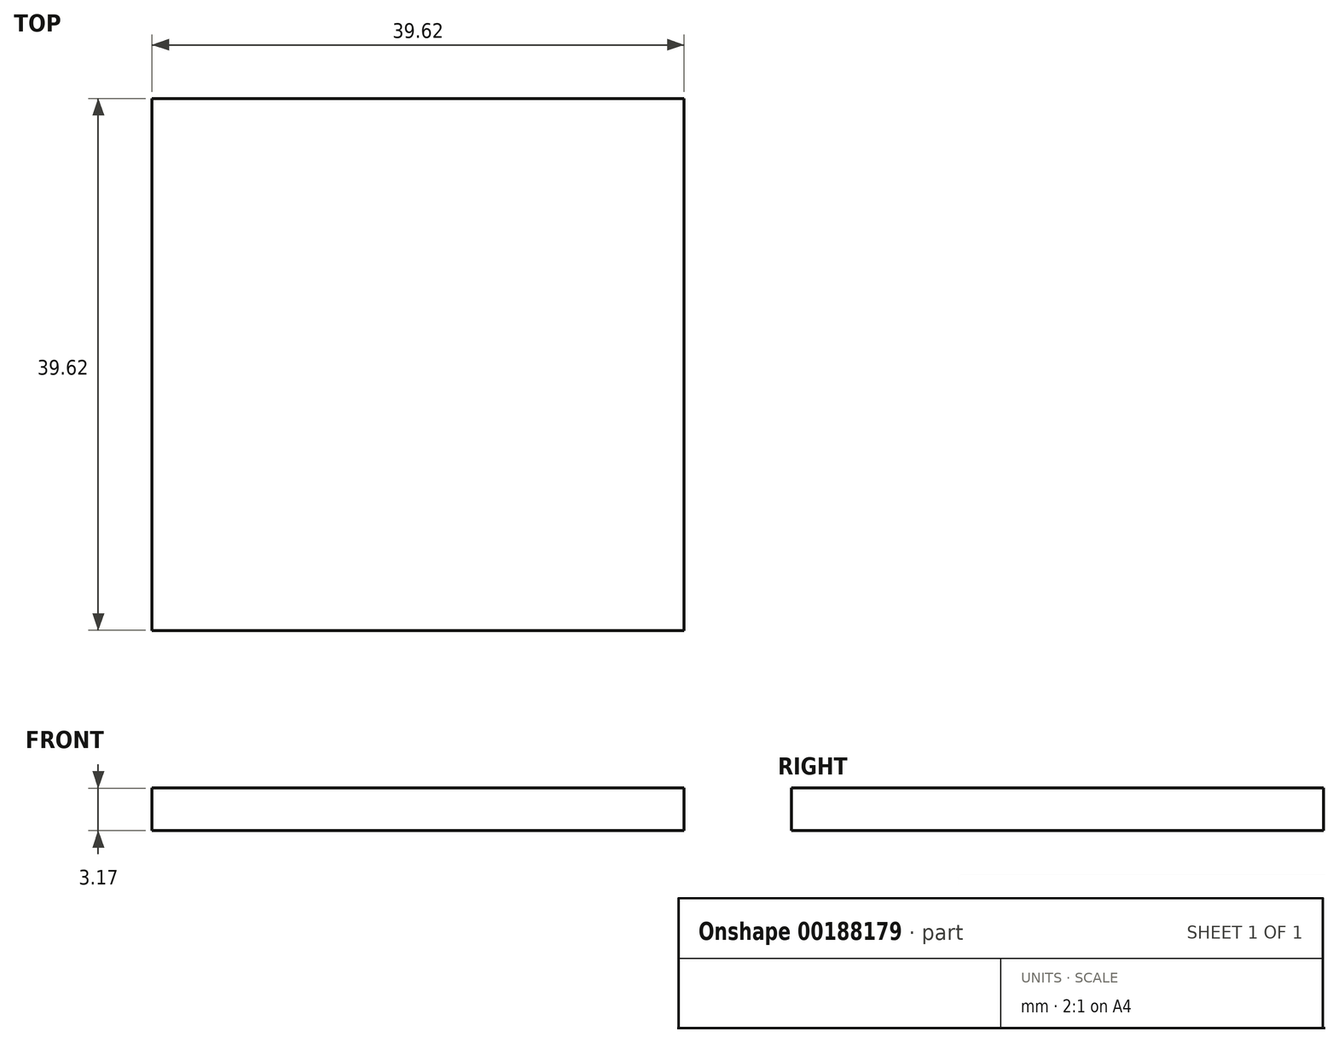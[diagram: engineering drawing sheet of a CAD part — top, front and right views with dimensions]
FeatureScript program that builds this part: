
annotation { "Feature Type Name" : "Feature", "Feature Type Description" : "" }
export const myFeature = defineFeature(function(context is Context, id is Id, definition is map)
    precondition{}
    {
        {
            var Q0;
            Q0=qCreatedBy(makeId("Top.planeOp"),FACE);
            var sketch = newSketch(context, id + "F0", { "sketchPlane" : qUnion([Q0])});
            skLineSegment(sketch, "E0.bottom", {"start": v(19.81, 19.81) * mm, "end": v(-19.81, 19.81) * mm});
            skLineSegment(sketch, "E0.top", {"start": v(19.81, -19.81) * mm, "end": v(-19.81, -19.81) * mm});
            skLineSegment(sketch, "E0.left", {"start": v(19.81, 19.81) * mm, "end": v(19.81, -19.81) * mm});
            skLineSegment(sketch, "E0.right", {"start": v(-19.81, 19.81) * mm, "end": v(-19.81, -19.81) * mm});
            skPoint(sketch, "E0.middle", {"position": v(0, 0) * mm});
            skSolve(sketch);
        }
        {
            var Q0;
            Q0=makeQuery(id+"F0.imprint","IMPRINT",FACE,{"disambiguationData":[TD([[makeQuery(id+"F0.imprint","IMPRINT",EDGE,{"derivedFrom":sQuery(id+"F0.wireOp",EDGE,"E0.bottom")}),1.0]])]});
            extrude(context, id + "F1", {"entities" : qUnion([Q0]), "depth" : 3.17 * mm});
        }
    });
